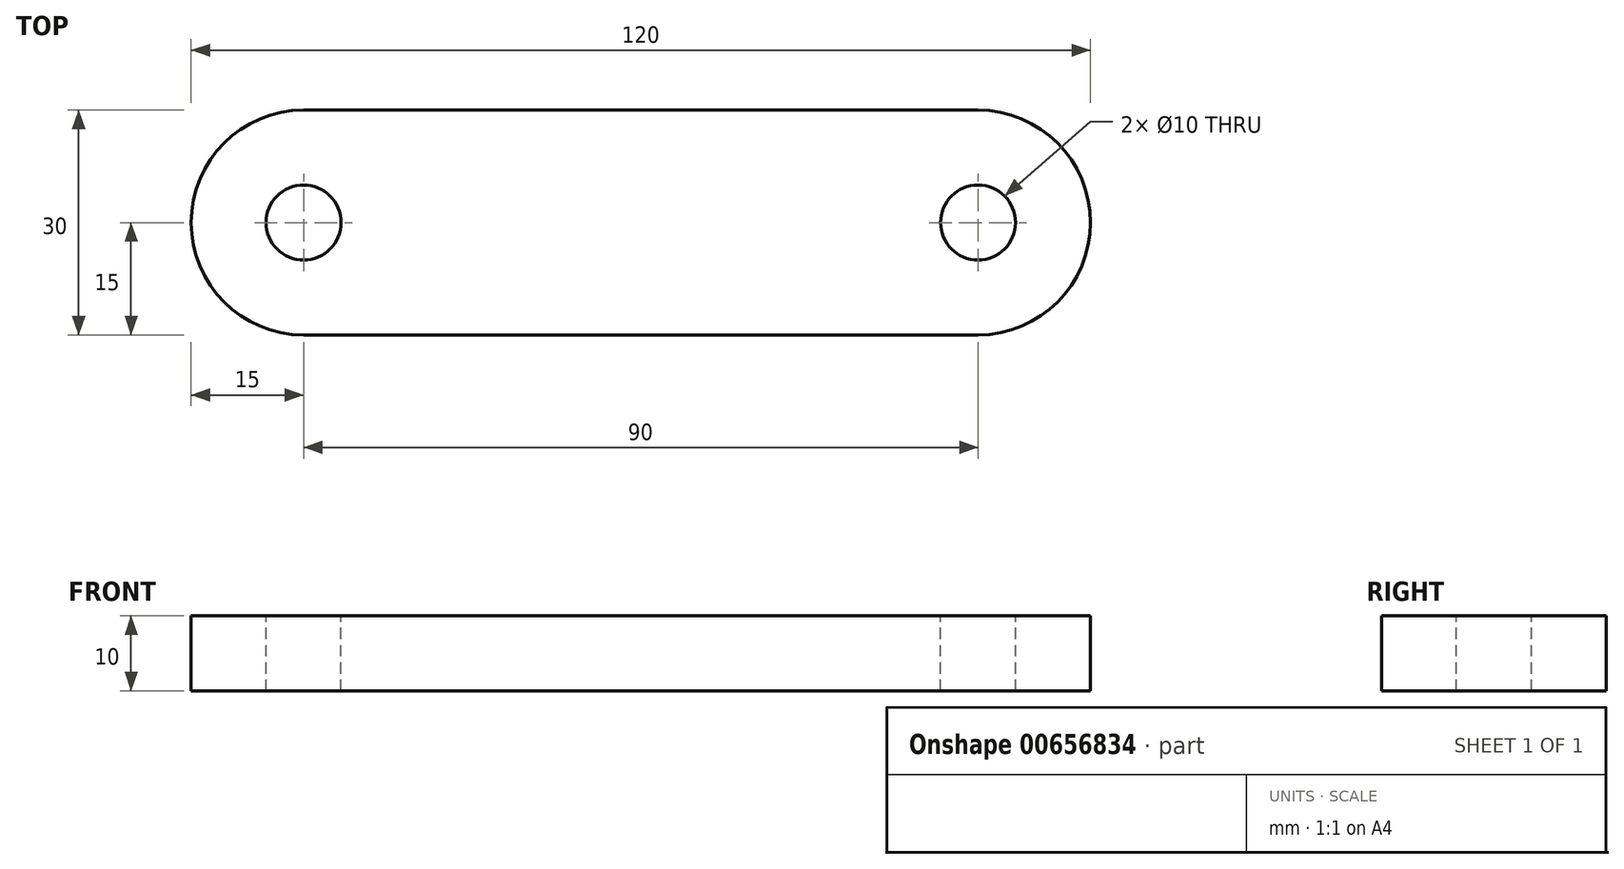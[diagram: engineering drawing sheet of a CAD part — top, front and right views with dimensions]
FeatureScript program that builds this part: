
annotation { "Feature Type Name" : "Feature", "Feature Type Description" : "" }
export const myFeature = defineFeature(function(context is Context, id is Id, definition is map)
    precondition{}
    {
        {
            var Q0;
            Q0=qCreatedBy(makeId("Top.planeOp"),FACE);
            var sketch = newSketch(context, id + "F0", { "sketchPlane" : qUnion([Q0])});
            skLineSegment(sketch, "E0.bottom", {"start": v(45, 15) * mm, "end": v(-45, 15) * mm});
            skLineSegment(sketch, "E0.top", {"start": v(45, -15) * mm, "end": v(-45, -15) * mm});
            skLineSegment(sketch, "E0.left", {"start": v(60, 0) * mm, "end": v(60, 0) * mm});
            skLineSegment(sketch, "E0.right", {"start": v(-60, 0) * mm, "end": v(-60, 0) * mm});
            skPoint(sketch, "E0.middle", {"position": v(0, 0) * mm});
            skPoint(sketch, "E1.visualSharp", {"position": v(-60, -15) * mm});
            skArc(sketch, "E1.filletArc", {"start": v(-60, 0) * mm, "mid": v(-55.6, -10.6) * mm, "end": v(-45, -15) * mm});
            skPoint(sketch, "E2.visualSharp", {"position": v(-60, 15) * mm});
            skArc(sketch, "E2.filletArc", {"start": v(-45, 15) * mm, "mid": v(-55.6, 10.6) * mm, "end": v(-60, 0) * mm});
            skPoint(sketch, "E3.visualSharp", {"position": v(60, -15) * mm});
            skArc(sketch, "E3.filletArc", {"start": v(45, -15) * mm, "mid": v(55.6, -10.6) * mm, "end": v(60, 0) * mm});
            skPoint(sketch, "E4.visualSharp", {"position": v(60, 15) * mm});
            skArc(sketch, "E4.filletArc", {"start": v(60, 0) * mm, "mid": v(55.6, 10.6) * mm, "end": v(45, 15) * mm});
            skSolve(sketch);
        }
        {
            var Q0;
            Q0 = qSketchRegion(id + "F0", true);
            extrude(context, id + "F1", {"entities" : qUnion([Q0]), "depth" : 10 * mm, "offsetDistance" : 25 * mm});
        }
        {
            var Q0;
            Q0=makeQuery(id+"F1.opExtrude","CAP_FACE",FACE,{"disambiguationData":[OSD([sQuery(id+"F0.wireOp",EDGE,"E0.bottom"),sQuery(id+"F0.wireOp",EDGE,"E0.top"),sQuery(id+"F0.wireOp",EDGE,"E1.filletArc"),sQuery(id+"F0.wireOp",EDGE,"E2.filletArc"),sQuery(id+"F0.wireOp",EDGE,"E3.filletArc"),sQuery(id+"F0.wireOp",EDGE,"E4.filletArc")])],"isStart":false});
            var sketch = newSketch(context, id + "F2", { "sketchPlane" : qUnion([Q0])});
            skCircle(sketch, "E5", {"center": v(-45, 0) * mm, "radius": 5 * mm});
            skCircle(sketch, "E6", {"center": v(45, 0) * mm, "radius": 5 * mm});
            skSolve(sketch);
        }
        {
            var Q0;
            Q0 = qSketchRegion(id + "F2", true);
            extrude(context, id + "F3", {"entities" : qUnion([Q0]), "operationType" : NewBodyOperationType.REMOVE, "oppositeDirection" : true, "depth" : 25 * mm, "offsetDistance" : 25 * mm});
        }
    });
